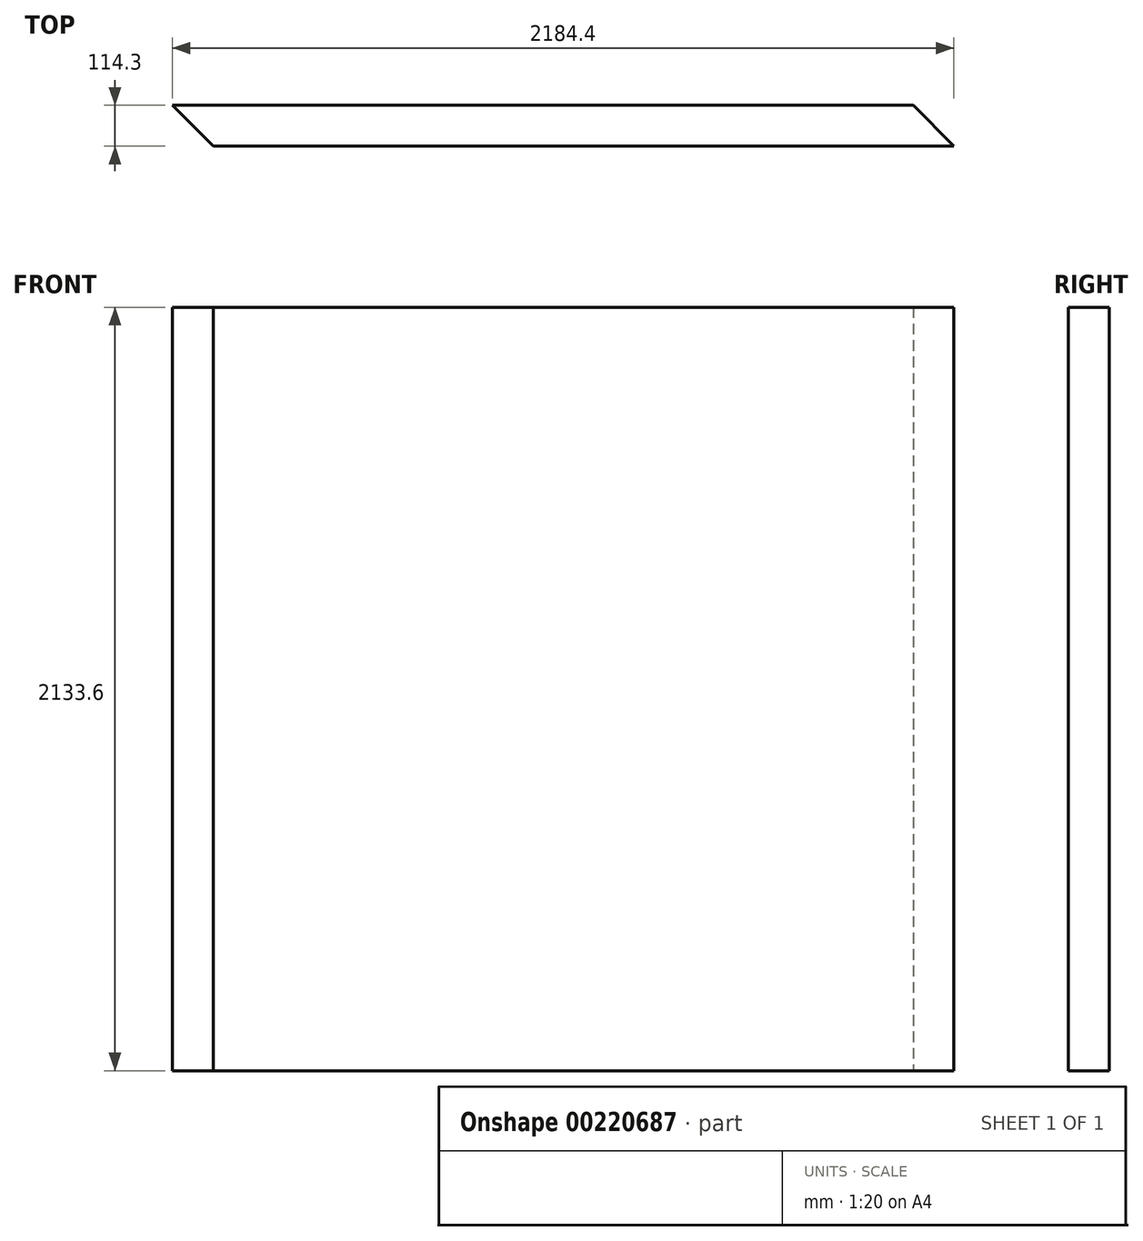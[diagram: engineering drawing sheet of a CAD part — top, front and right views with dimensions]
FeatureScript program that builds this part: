
annotation { "Feature Type Name" : "Feature", "Feature Type Description" : "" }
export const myFeature = defineFeature(function(context is Context, id is Id, definition is map)
    precondition{}
    {
        {
            var Q0;
            Q0=qCreatedBy(makeId("Top.planeOp"),FACE);
            var sketch = newSketch(context, id + "F0", { "sketchPlane" : qUnion([Q0])});
            skLineSegment(sketch, "E0.bottom", {"start": v(977.9, -57.15) * mm, "end": v(-977.9, -57.15) * mm});
            skLineSegment(sketch, "E0.top", {"start": v(977.9, 57.15) * mm, "end": v(-977.9, 57.15) * mm});
            skLineSegment(sketch, "E0.left", {"start": v(977.9, -57.15) * mm, "end": v(977.9, 57.15) * mm});
            skLineSegment(sketch, "E0.right", {"start": v(-977.9, -57.15) * mm, "end": v(-977.9, 57.15) * mm});
            skPoint(sketch, "E0.middle", {"position": v(0, 0) * mm});
            skLineSegment(sketch, "E1", {"start": v(977.9, -57.15) * mm, "end": v(1092.2, -57.15) * mm});
            skLineSegment(sketch, "E2", {"start": v(1092.2, -57.15) * mm, "end": v(977.9, 57.15) * mm});
            skLineSegment(sketch, "E3", {"start": v(-977.9, 57.15) * mm, "end": v(-1092.2, 57.15) * mm});
            skLineSegment(sketch, "E4", {"start": v(-1092.2, 57.15) * mm, "end": v(-977.9, -57.15) * mm});
            skSolve(sketch);
        }
        {
            var Q0;
            Q0 = qSketchRegion(id + "F0", true);
            extrude(context, id + "F1", {"entities" : qUnion([Q0]), "endBound" : BoundingType.SYMMETRIC, "depth" : 2133.6 * mm});
        }
    });
